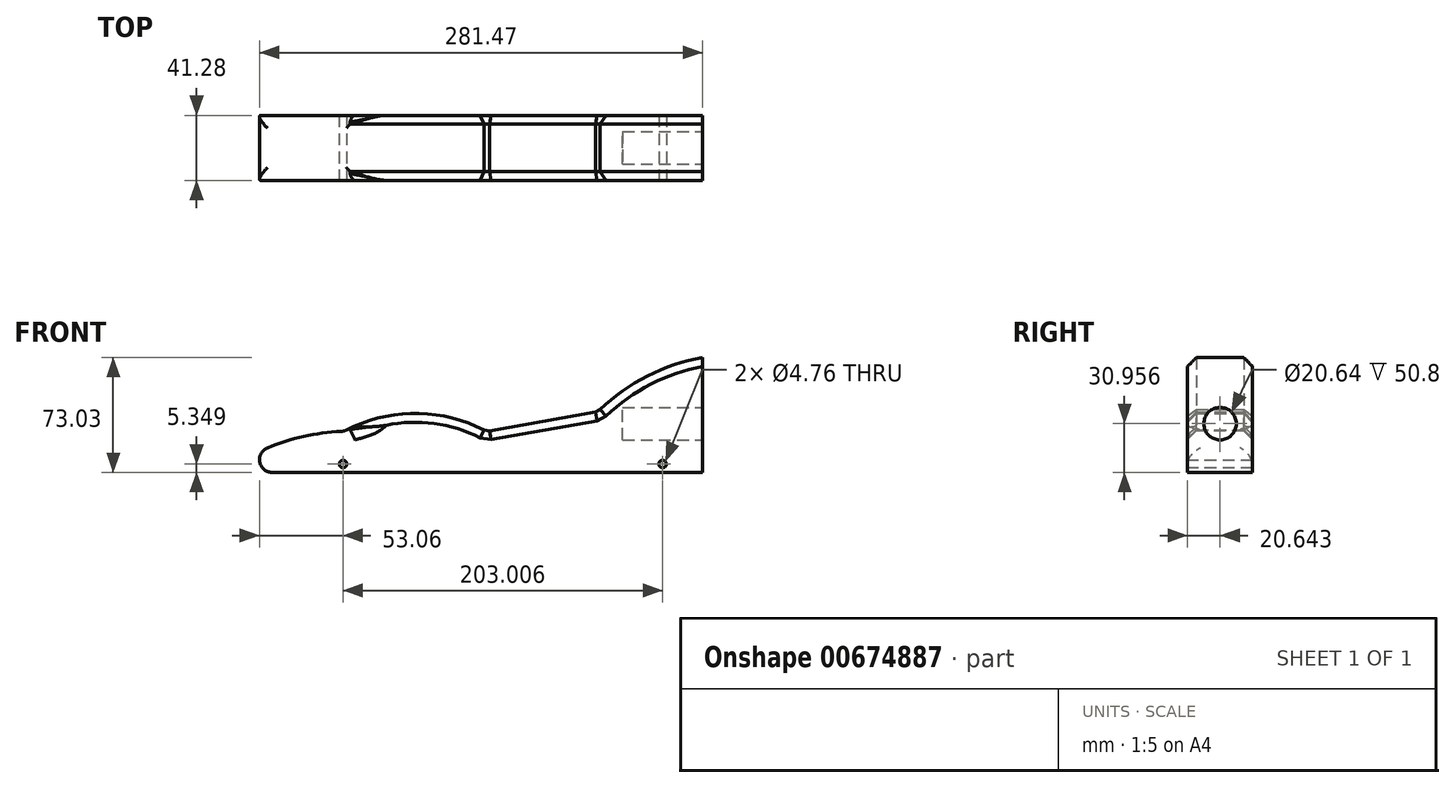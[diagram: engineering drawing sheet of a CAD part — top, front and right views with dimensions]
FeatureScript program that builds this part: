
annotation { "Feature Type Name" : "Feature", "Feature Type Description" : "" }
export const myFeature = defineFeature(function(context is Context, id is Id, definition is map)
    precondition{}
    {
        {
            var Q0;
            Q0=qCreatedBy(makeId("Front.planeOp"),FACE);
            var sketch = newSketch(context, id + "F0", { "sketchPlane" : qUnion([Q0])});
            skLineSegment(sketch, "E0", {"start": v(-153.67, 0) * mm, "end": v(151.13, 0) * mm});
            skLineSegment(sketch, "E1", {"start": v(151.13, 0) * mm, "end": v(151.13, 73.03) * mm});
            skLineSegment(sketch, "E2", {"start": v(151.13, 73.03) * mm, "end": v(-153.67, 19.05) * mm});
            skLineSegment(sketch, "E3", {"start": v(-153.67, 19.05) * mm, "end": v(-153.67, 0) * mm});
            skSolve(sketch);
        }
        {
            var Q0;
            Q0=makeQuery(id+"F0.imprint","IMPRINT",FACE,{"disambiguationData":[TD([[makeQuery(id+"F0.imprint","IMPRINT",EDGE,{"derivedFrom":sQuery(id+"F0.wireOp",EDGE,"E0")}),1.0]])]});
            extrude(context, id + "F1", {"entities" : qUnion([Q0]), "depth" : 41.27 * mm, "offsetDistance" : 25.4 * mm});
        }
        {
            var Q0;
            Q0=makeQuery(id+"F1.opExtrude","SWEPT_FACE",FACE,{"disambiguationData":[OSD([sQuery(id+"F0.wireOp",EDGE,"E1")])]});
            var sketch = newSketch(context, id + "F2", { "sketchPlane" : qUnion([Q0])});
            skLineSegment(sketch, "E4", {"start": v(-20.64, 0) * mm, "end": v(-20.64, 20.64) * mm});
            skLineSegment(sketch, "E5", {"start": v(-20.64, 73.03) * mm, "end": v(-20.64, 41.28) * mm});
            skLineSegment(sketch, "E6", {"start": v(-20.64, 41.28) * mm, "end": v(-20.64, 20.64) * mm});
            skLineSegment(sketch, "E7", {"start": v(-20.64, 41.28) * mm, "end": v(-20.64, 30.96) * mm});
            skCircle(sketch, "E8", {"center": v(-20.64, 30.96) * mm, "radius": 10.32 * mm});
            skSolve(sketch);
        }
        {
            var Q0;
            {var subQ0=sQuery(id+"F2.wireOp",EDGE,"E6");Q0=makeQuery(id+"F2.imprint","IMPRINT",FACE,{"disambiguationData":[TD([[makeQuery(id+"F2.imprint","IMPRINT",EDGE,{"derivedFrom":subQ0}),-1.0]])]});}
            var Q1;
            {var subQ0=sQuery(id+"F2.wireOp",EDGE,"E6");Q1=makeQuery(id+"F2.imprint","IMPRINT",FACE,{"disambiguationData":[TD([[makeQuery(id+"F2.imprint","IMPRINT",EDGE,{"derivedFrom":subQ0}),1.0]])]});}
            extrude(context, id + "F3", {"entities" : qUnion([Q0, Q1]), "operationType" : NewBodyOperationType.REMOVE, "oppositeDirection" : true, "depth" : 50.8 * mm, "offsetDistance" : 25.4 * mm});
        }
        {
            var Q0;
            Q0=qCreatedBy(makeId("Front.planeOp"),FACE);
            var sketch = newSketch(context, id + "F4", { "sketchPlane" : qUnion([Q0])});
            skLineSegment(sketch, "E9.0", {"start": v(151.13, 73.03) * mm, "end": v(-153.67, 19.05) * mm});
            skLineSegment(sketch, "E10.0", {"start": v(-153.67, 19.05) * mm, "end": v(-153.67, 0) * mm});
            skLineSegment(sketch, "E11.0", {"start": v(-153.67, 0) * mm, "end": v(151.13, 0) * mm});
            skLineSegment(sketch, "E12.0", {"start": v(151.13, 0) * mm, "end": v(151.13, 73.03) * mm});
            skArc(sketch, "E13", {"start": v(-76.68, 26.16) * mm, "mid": v(-117.11, 18.77) * mm, "end": v(-153.67, 0) * mm});
            skArc(sketch, "E14", {"start": v(13.94, 26.16) * mm, "mid": v(-31.37, 37.5) * mm, "end": v(-76.68, 26.16) * mm});
            skLineSegment(sketch, "E15", {"start": v(13.94, 26.16) * mm, "end": v(84.72, 38.7) * mm});
            skArc(sketch, "E16", {"start": v(151.13, 73.02) * mm, "mid": v(115.31, 60.9) * mm, "end": v(84.72, 38.7) * mm});
            skLineSegment(sketch, "E17", {"start": v(151.13, 73.03) * mm, "end": v(151.13, 0) * mm});
            skSolve(sketch);
        }
        {
            var Q0;
            Q0=makeQuery(id+"F4.imprint","IMPRINT",FACE,{"disambiguationData":[TD([[makeQuery(id+"F4.imprint","IMPRINT",EDGE,{"derivedFrom":sQuery(id+"F4.wireOp",EDGE,"E9.0")}),1.0]])]});
            extrude(context, id + "F5", {"entities" : qUnion([Q0]), "operationType" : NewBodyOperationType.REMOVE, "depth" : 139.7 * mm, "offsetDistance" : 25.4 * mm});
        }
        {
            var Q0;
            Q0=makeQuery(id+"F5.boolean.opBoolean","COPY",FACE,{"derivedFrom":makeQuery(id+"F5.opExtrude","SWEPT_FACE",FACE,{"disambiguationData":[OSD([sQuery(id+"F4.wireOp",EDGE,"E15")])]})});
            chamfer(context, id + "F6", {"entities" : qUnion([Q0]), "width" : 5.64 * mm, "tangentPropagation" : true});
        }
        {
            var Q0;
            Q0=makeQuery(id+"F5.boolean.opBoolean","COPY",FACE,{"derivedFrom":makeQuery(id+"F5.opExtrude","SWEPT_FACE",FACE,{"disambiguationData":[OSD([sQuery(id+"F4.wireOp",EDGE,"E13")])]})});
            fillet(context, id + "F7", {"entities" : qUnion([Q0]), "radius" : 8.16 * mm, "tangentPropagation" : true, "allowEdgeOverflow" : false});
        }
        {
            var Q0;
            Q0=makeQuery(id+"F1.opExtrude","CAP_FACE",FACE,{"disambiguationData":[OSD([sQuery(id+"F0.wireOp",EDGE,"E0"),sQuery(id+"F0.wireOp",EDGE,"E1"),sQuery(id+"F0.wireOp",EDGE,"E2"),sQuery(id+"F0.wireOp",EDGE,"E3")])],"isStart":false});
            var sketch = newSketch(context, id + "F8", { "sketchPlane" : qUnion([Q0])});
            skLineSegment(sketch, "E18", {"start": v(151.13, 5.35) * mm, "end": v(125.73, 5.35) * mm});
            skLineSegment(sketch, "E19", {"start": v(-128.55, 5.35) * mm, "end": v(-77.28, 5.35) * mm});
            skCircle(sketch, "E20", {"center": v(-77.28, 5.35) * mm, "radius": 2.38 * mm});
            skCircle(sketch, "E21", {"center": v(125.73, 5.35) * mm, "radius": 2.38 * mm});
            skSolve(sketch);
        }
        {
            var Q0;
            Q0=makeQuery(id+"F8.imprint","IMPRINT",FACE,{"disambiguationData":[TD([[makeQuery(id+"F8.imprint","IMPRINT",EDGE,{"derivedFrom":sQuery(id+"F8.wireOp",EDGE,"E21")}),1.0]])]});
            var Q1;
            Q1=makeQuery(id+"F8.imprint","IMPRINT",FACE,{"disambiguationData":[TD([[makeQuery(id+"F8.imprint","IMPRINT",EDGE,{"derivedFrom":sQuery(id+"F8.wireOp",EDGE,"E20")}),1.0]])]});
            extrude(context, id + "F9", {"entities" : qUnion([Q0, Q1]), "operationType" : NewBodyOperationType.REMOVE, "oppositeDirection" : true, "depth" : 50.8 * mm, "offsetDistance" : 25.4 * mm});
        }
    });
